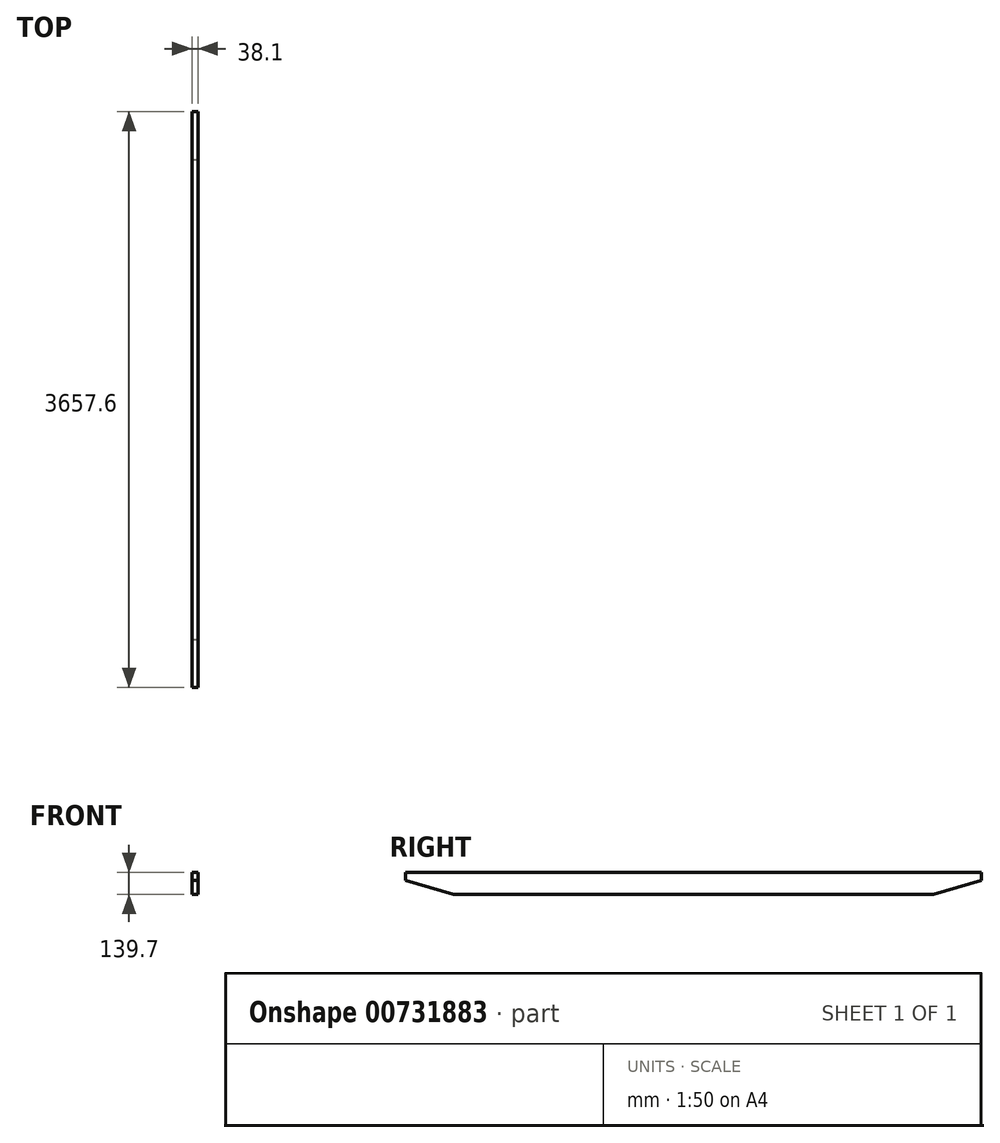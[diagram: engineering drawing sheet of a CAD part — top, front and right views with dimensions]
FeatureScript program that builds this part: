
annotation { "Feature Type Name" : "Feature", "Feature Type Description" : "" }
export const myFeature = defineFeature(function(context is Context, id is Id, definition is map)
    precondition{}
    {
        {
            var Q0;
            Q0=qCreatedBy(makeId("Front.planeOp"),FACE);
            var sketch = newSketch(context, id + "F0", { "sketchPlane" : qUnion([Q0])});
            skLineSegment(sketch, "E0.bottom", {"start": v(0, 0) * mm, "end": v(38.1, 0) * mm});
            skLineSegment(sketch, "E0.top", {"start": v(0, 139.7) * mm, "end": v(38.1, 139.7) * mm});
            skLineSegment(sketch, "E0.left", {"start": v(0, 0) * mm, "end": v(0, 139.7) * mm});
            skLineSegment(sketch, "E0.right", {"start": v(38.1, 0) * mm, "end": v(38.1, 139.7) * mm});
            skSolve(sketch);
        }
        {
            var Q0;
            Q0=makeQuery(id+"F0.imprint","IMPRINT",FACE,{"disambiguationData":[TD([[makeQuery(id+"F0.imprint","IMPRINT",EDGE,{"derivedFrom":sQuery(id+"F0.wireOp",EDGE,"E0.bottom")}),1.0]])]});
            extrude(context, id + "F1", {"entities" : qUnion([Q0]), "depth" : 3657.6 * mm, "offsetDistance" : 25.4 * mm});
        }
        {
            var Q0;
            Q0=makeQuery(id+"F1.opExtrude","SWEPT_FACE",FACE,{"disambiguationData":[OSD([sQuery(id+"F0.wireOp",EDGE,"E0.right")])]});
            var sketch = newSketch(context, id + "F2", { "sketchPlane" : qUnion([Q0])});
            skLineSegment(sketch, "E1", {"start": v(-3657.6, 0) * mm, "end": v(-3352.8, 0) * mm});
            skLineSegment(sketch, "E2", {"start": v(-3352.8, 0) * mm, "end": v(-3657.6, 88.9) * mm});
            skLineSegment(sketch, "E3", {"start": v(-3657.6, 88.9) * mm, "end": v(-3657.6, 0) * mm});
            skLineSegment(sketch, "E4", {"start": v(0, 0) * mm, "end": v(0, 88.9) * mm});
            skLineSegment(sketch, "E5", {"start": v(0, 88.9) * mm, "end": v(-304.8, 0) * mm});
            skLineSegment(sketch, "E6", {"start": v(-304.8, 0) * mm, "end": v(0, 0) * mm});
            skPoint(sketch, "E7", {"position": v(-3200.4, 0) * mm});
            skPoint(sketch, "E8", {"position": v(-457.2, 0) * mm});
            skSolve(sketch);
        }
        {
            var Q0;
            Q0=makeQuery(id+"F2.imprint","IMPRINT",FACE,{"disambiguationData":[TD([[makeQuery(id+"F2.imprint","IMPRINT",EDGE,{"derivedFrom":sQuery(id+"F2.wireOp",EDGE,"E1")}),1.0]])]});
            var Q1;
            Q1=makeQuery(id+"F2.imprint","IMPRINT",FACE,{"disambiguationData":[TD([[makeQuery(id+"F2.imprint","IMPRINT",EDGE,{"derivedFrom":sQuery(id+"F2.wireOp",EDGE,"E4")}),1.0]])]});
            extrude(context, id + "F3", {"entities" : qUnion([Q0, Q1]), "operationType" : NewBodyOperationType.REMOVE, "endBound" : BoundingType.THROUGH_ALL, "oppositeDirection" : true, "depth" : 25.4 * mm, "offsetDistance" : 25.4 * mm});
        }
        {
            var Q0;
            Q0=makeQuery(id+"F1.opExtrude","SWEPT_FACE",FACE,{"disambiguationData":[OSD([sQuery(id+"F0.wireOp",EDGE,"E0.right")])]});
            var sketch = newSketch(context, id + "F4", { "sketchPlane" : qUnion([Q0])});
            skLineSegment(sketch, "E9", {"start": v(-3281.43, 0) * mm, "end": v(-3274.76, 59.96) * mm});
            skLineSegment(sketch, "E10", {"start": v(-3274.76, 59.96) * mm, "end": v(-3135.92, 44.53) * mm});
            skLineSegment(sketch, "E11", {"start": v(-3135.92, 44.53) * mm, "end": v(-3140.87, 0) * mm});
            skLineSegment(sketch, "E12", {"start": v(-3140.87, 0) * mm, "end": v(-3281.43, 0) * mm});
            skSolve(sketch);
        }
    });
